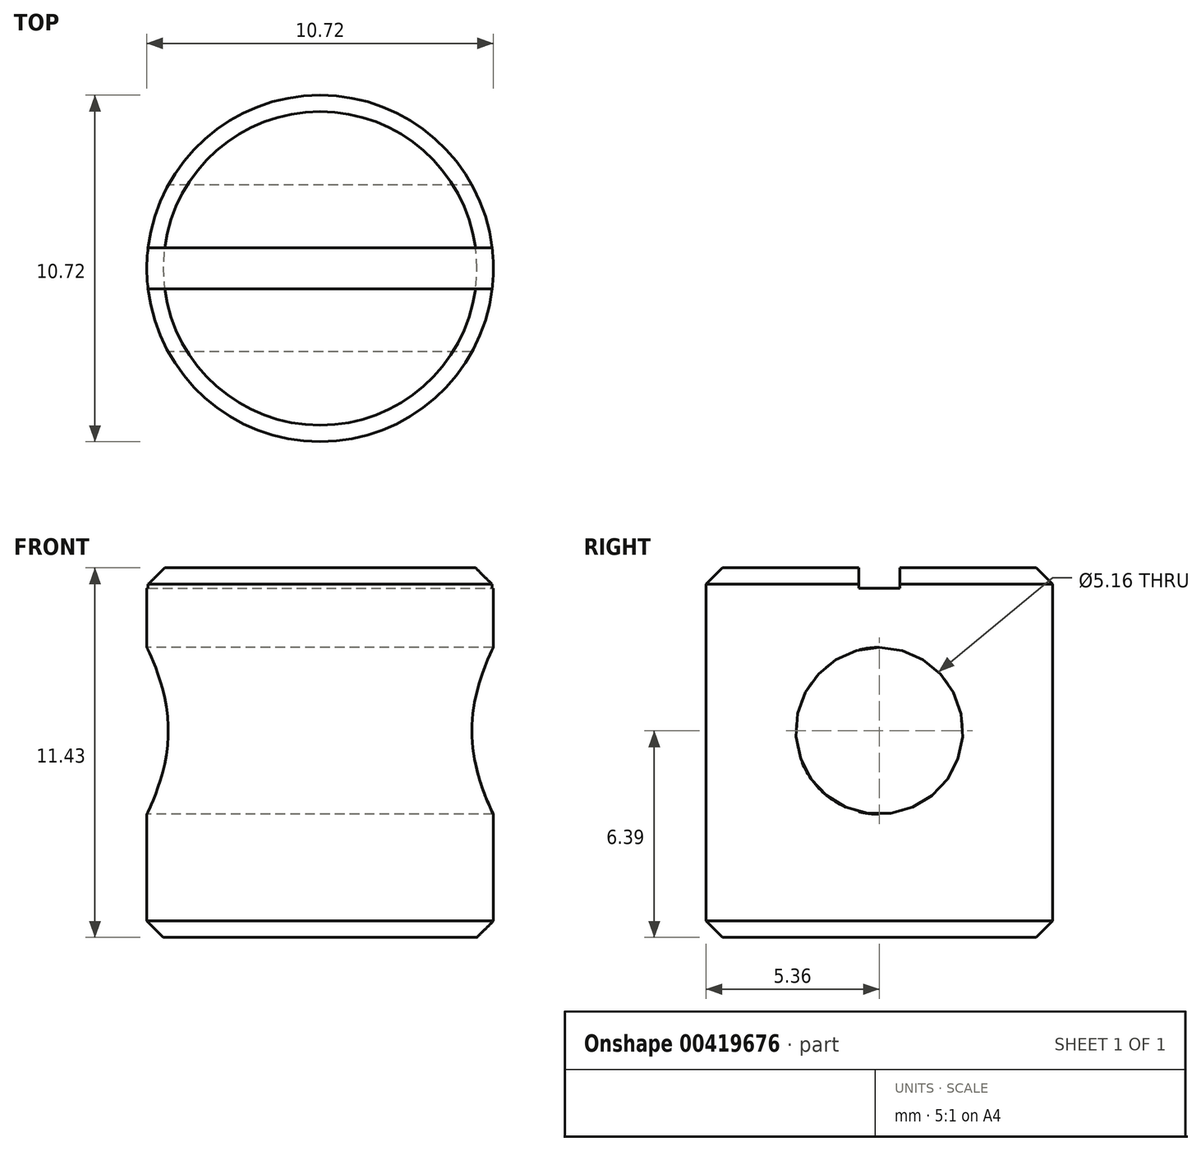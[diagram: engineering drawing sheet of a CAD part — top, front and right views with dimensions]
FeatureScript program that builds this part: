
annotation { "Feature Type Name" : "Feature", "Feature Type Description" : "" }
export const myFeature = defineFeature(function(context is Context, id is Id, definition is map)
    precondition{}
    {
        {
            var Q0;
            Q0=qCreatedBy(makeId("Top.planeOp"),FACE);
            var sketch = newSketch(context, id + "F0", { "sketchPlane" : qUnion([Q0])});
            skCircle(sketch, "E0", {"center": v(0, 0) * mm, "radius": 5.36 * mm});
            skSolve(sketch);
        }
        {
            var Q0;
            Q0=qSketchRegion(id+"F0",true);
            extrude(context, id + "F1", {"entities" : qUnion([Q0]), "depth" : 11.43 * mm, "offsetDistance" : 25.4 * mm});
        }
        {
            var Q0;
            Q0=qCreatedBy(makeId("Right.planeOp"),FACE);
            var sketch = newSketch(context, id + "F2", { "sketchPlane" : qUnion([Q0])});
            skCircle(sketch, "E1", {"center": v(0, 6.39) * mm, "radius": 2.58 * mm});
            skSolve(sketch);
        }
        {
            var Q0;
            Q0=qSketchRegion(id+"F2",true);
            extrude(context, id + "F3", {"entities" : qUnion([Q0]), "operationType" : NewBodyOperationType.REMOVE, "depth" : 25.4 * mm, "offsetDistance" : 25.4 * mm, "hasSecondDirection" : true, "secondDirectionOppositeDirection" : true, "secondDirectionDepth" : 25.4 * mm});
        }
        {
            var Q0;
            Q0=makeQuery(id+"F1.opExtrude","CAP_FACE",FACE,{"disambiguationData":[OSD([sQuery(id+"F0.wireOp",EDGE,"E0")])],"isStart":false});
            var sketch = newSketch(context, id + "F4", { "sketchPlane" : qUnion([Q0])});
            skLineSegment(sketch, "E2", {"start": v(-5.32, 0) * mm, "end": v(5.32, 0) * mm});
            skLineSegment(sketch, "E3", {"start": v(-5.32, 0.64) * mm, "end": v(5.32, 0.64) * mm});
            skLineSegment(sketch, "E4.MirrorCS", {"start": v(-5.32, -0.64) * mm, "end": v(5.32, -0.64) * mm});
            skArc(sketch, "E5", {"start": v(-5.32, 0.63) * mm, "mid": v(-5.38, 0) * mm, "end": v(-5.32, -0.64) * mm});
            skArc(sketch, "E6.MirrorCS", {"start": v(5.32, 0.63) * mm, "mid": v(5.38, 0) * mm, "end": v(5.32, -0.64) * mm});
            skSolve(sketch);
        }
        {
            var Q0;
            Q0 = qSketchRegion(id + "F4", true);
            extrude(context, id + "F5", {"entities" : qUnion([Q0]), "operationType" : NewBodyOperationType.REMOVE, "oppositeDirection" : true, "depth" : 0.64 * mm, "offsetDistance" : 25.4 * mm});
        }
        {
            var Q0;
            {var subQ0=sQuery(id+"F0.wireOp",EDGE,"E0");Q0=makeQuery(id+"F5.boolean.opBoolean","SPLIT",EDGE,{"disambiguationData":[TD([makeQuery(id+"F5.opExtrude","SWEPT_FACE",FACE,{"disambiguationData":[OSD([sQuery(id+"F4.wireOp",EDGE,"E4.MirrorCS")])]})])],"derivedFrom":makeQuery(id+"F1.opExtrude","CAP_EDGE",EDGE,{"disambiguationData":[OSD([subQ0])],"isStart":false})});}
            var Q1;
            {var subQ0=sQuery(id+"F0.wireOp",EDGE,"E0");Q1=makeQuery(id+"F5.boolean.opBoolean","SPLIT",EDGE,{"disambiguationData":[TD([makeQuery(id+"F5.opExtrude","SWEPT_FACE",FACE,{"disambiguationData":[OSD([sQuery(id+"F4.wireOp",EDGE,"E3")])]})])],"derivedFrom":makeQuery(id+"F1.opExtrude","CAP_EDGE",EDGE,{"disambiguationData":[OSD([subQ0])],"isStart":false})});}
            var Q2;
            Q2=makeQuery(id+"F1.opExtrude","CAP_EDGE",EDGE,{"disambiguationData":[OSD([sQuery(id+"F0.wireOp",EDGE,"E0")])],"isStart":true});
            chamfer(context, id + "F6", {"entities" : qUnion([Q0, Q1, Q2]), "width" : 0.5 * mm, "tangentPropagation" : true});
        }
    });
